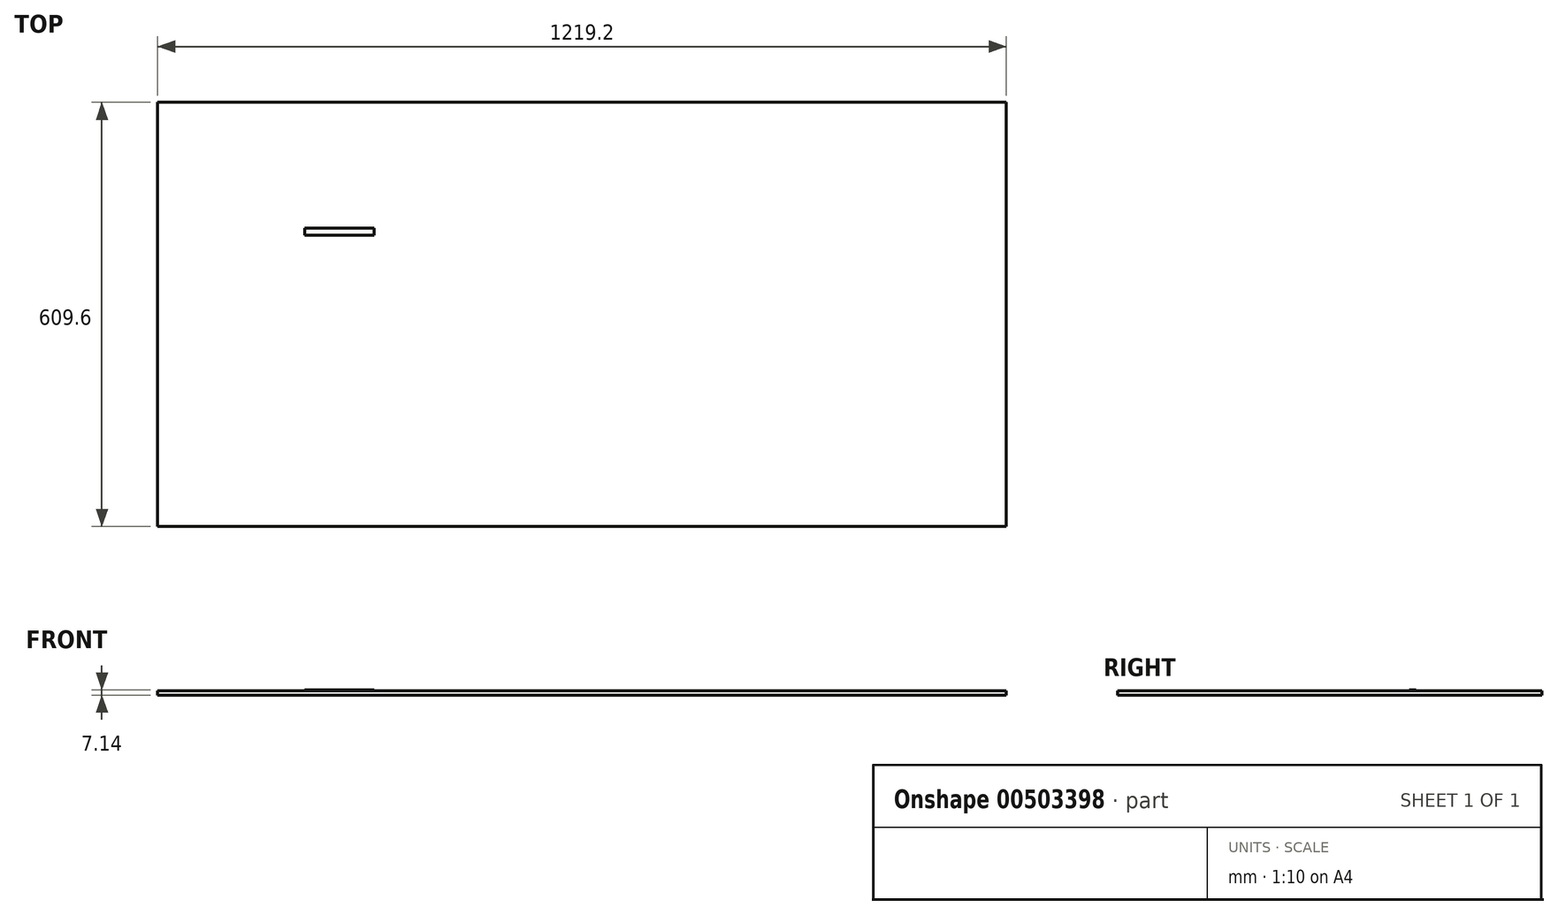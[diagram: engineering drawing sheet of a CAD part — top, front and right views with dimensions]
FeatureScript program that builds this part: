
annotation { "Feature Type Name" : "Feature", "Feature Type Description" : "" }
export const myFeature = defineFeature(function(context is Context, id is Id, definition is map)
    precondition{}
    {
        {
            var Q0;
            Q0=qCreatedBy(makeId("Top.planeOp"),FACE);
            var sketch = newSketch(context, id + "F0", { "sketchPlane" : qUnion([Q0])});
            skLineSegment(sketch, "E0.bottom", {"start": v(609.6, 304.8) * mm, "end": v(-609.6, 304.8) * mm});
            skLineSegment(sketch, "E0.top", {"start": v(609.6, -304.8) * mm, "end": v(-609.6, -304.8) * mm});
            skLineSegment(sketch, "E0.left", {"start": v(609.6, 304.8) * mm, "end": v(609.6, -304.8) * mm});
            skLineSegment(sketch, "E0.right", {"start": v(-609.6, 304.8) * mm, "end": v(-609.6, -304.8) * mm});
            skPoint(sketch, "E0.middle", {"position": v(0, 0) * mm});
            skSolve(sketch);
        }
        {
            var Q0;
            Q0 = qSketchRegion(id + "F0", true);
            extrude(context, id + "F1", {"entities" : qUnion([Q0]), "depth" : 6.35 * mm, "offsetDistance" : 25.4 * mm});
        }
        {
            var Q0;
            Q0=makeQuery(id+"F1.opExtrude","CAP_FACE",FACE,{"disambiguationData":[OSD([sQuery(id+"F0.wireOp",EDGE,"E0.bottom"),sQuery(id+"F0.wireOp",EDGE,"E0.top"),sQuery(id+"F0.wireOp",EDGE,"E0.left"),sQuery(id+"F0.wireOp",EDGE,"E0.right")])],"isStart":false});
            var sketch = newSketch(context, id + "F2", { "sketchPlane" : qUnion([Q0])});
            skLineSegment(sketch, "E1.bottom", {"start": v(-398.5, 113.86) * mm, "end": v(-298.5, 113.86) * mm});
            skLineSegment(sketch, "E1.top", {"start": v(-398.5, 123.86) * mm, "end": v(-298.5, 123.86) * mm});
            skLineSegment(sketch, "E1.left", {"start": v(-398.5, 113.86) * mm, "end": v(-398.5, 123.86) * mm});
            skLineSegment(sketch, "E1.right", {"start": v(-298.5, 113.86) * mm, "end": v(-298.5, 123.86) * mm});
            skSolve(sketch);
        }
        {
            var Q0;
            Q0 = qSketchRegion(id + "F2", true);
            extrude(context, id + "F3", {"entities" : qUnion([Q0]), "depth" : 0.8 * mm, "offsetDistance" : 25.4 * mm});
        }
    });
